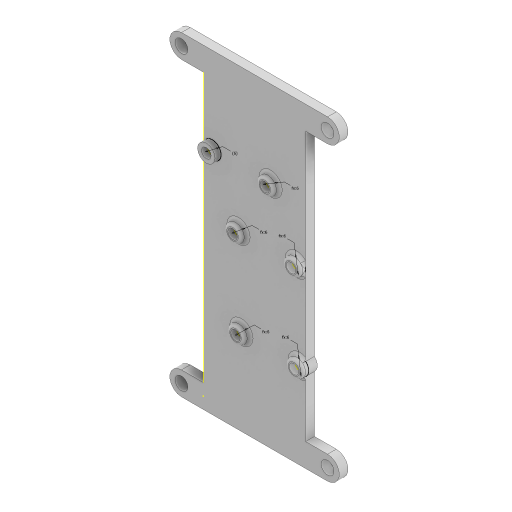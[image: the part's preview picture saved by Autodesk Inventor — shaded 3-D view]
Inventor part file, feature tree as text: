
AUTODESK INVENTOR PART (.ipt)
format: ipt  version: 2023 (Build 270158000, 158)  size: 239,616 bytes
history: native  units: mm
features: extrude x3, sketch x2, fillet x1
ambient origin geometry x8: Origin, YZ Plane, XZ Plane, XY Plane, X Axis, Y Axis, Z Axis, Center Point
bodies: Solid1 (feature_tree)
feature tree (6):
  extrude  "Extrusion1"  Depth=100.0mm
  sketch  "Sketch2"  dims[d2=50.0mm d3=8.0mm d4=8.0mm d5=50.0mm d7=7.5mm d8=4.4mm d9=4.4mm d10=4.4mm d11=4.4mm d12=15.0mm d13=55.0mm d14=2.5mm d15=0.0mm d16=3.0mm d17=3.0mm d18=22.5mm d19=12.0mm d20=13.0mm d21=52.0mm d22=3.3mm d23=3.3mm d24=3.3mm d25=20.0mm d27=20.0mm d28=10.0mm d30=10.0mm d32=3.0mm d33=0.0mm d34=6.0mm d35=6.0mm d36=6.0mm d37=6.0mm d38=6.0mm d39=6.0mm d40=2.0mm d41=0.0mm d42=3.0mm d43=0.0mm d44=1.0mm]
  extrude  "Extrusion2"  Depth=1.0mm
  extrude  "Extrusion3"  Depth=1.0mm
  fillet  "Fillet1"  Radius=50.0mm
  sketch  "Sketch1"  dims[d0=35.0mm d1=100.0mm]
